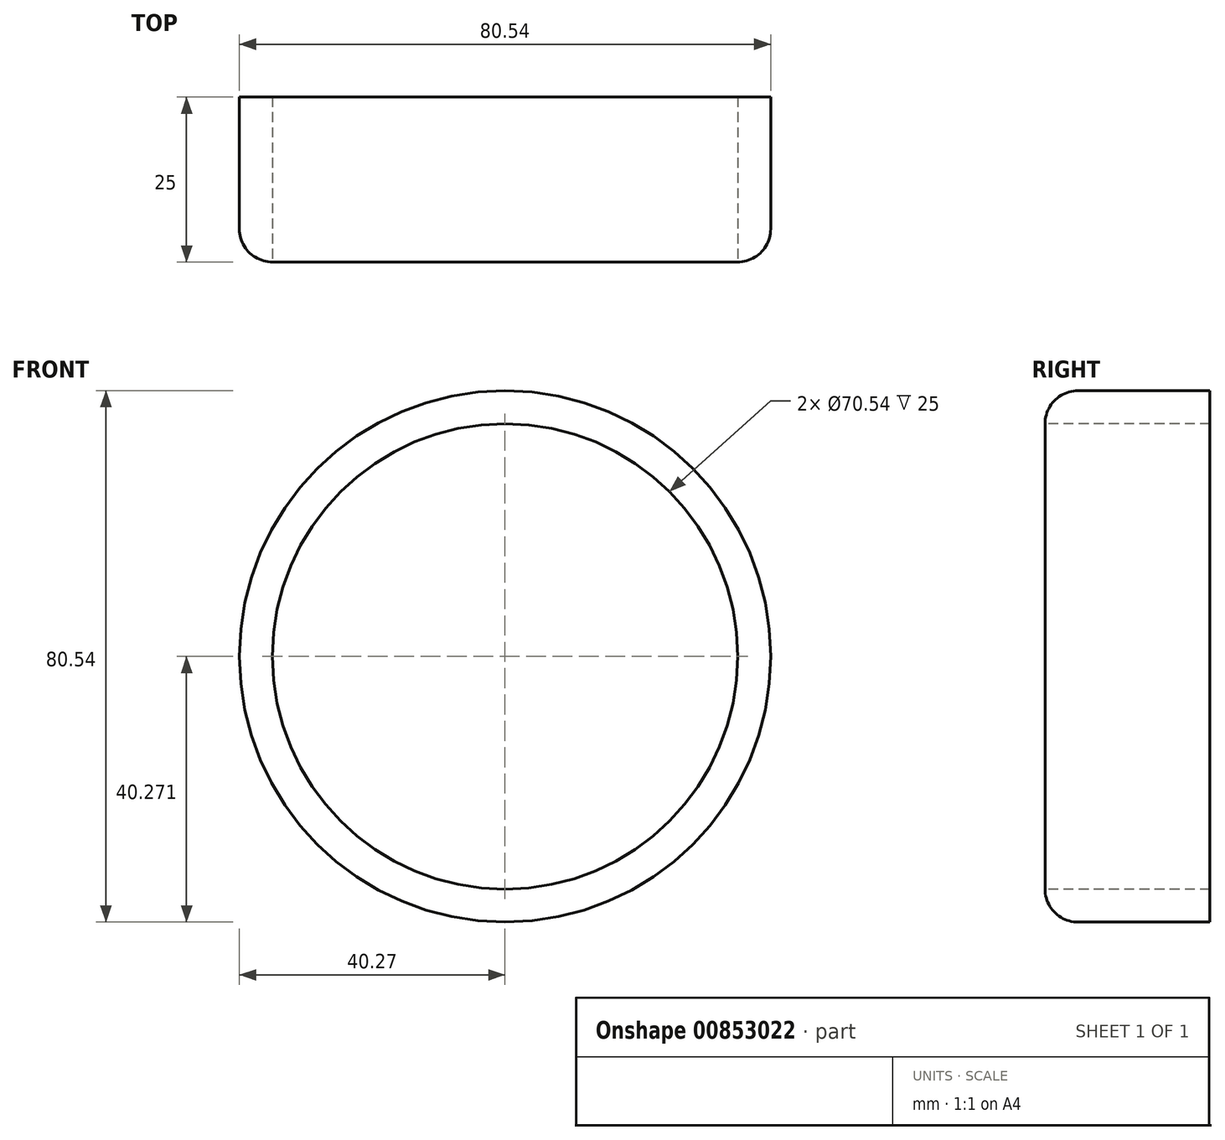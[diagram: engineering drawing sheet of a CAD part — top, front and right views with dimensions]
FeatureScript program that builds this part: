
annotation { "Feature Type Name" : "Feature", "Feature Type Description" : "" }
export const myFeature = defineFeature(function(context is Context, id is Id, definition is map)
    precondition{}
    {
        {
            var Q0;
            Q0=qCreatedBy(makeId("Front.planeOp"),FACE);
            var sketch = newSketch(context, id + "F0", { "sketchPlane" : qUnion([Q0])});
            skCircle(sketch, "E0", {"center": v(0, -5.18) * mm, "radius": 40.27 * mm});
            skSolve(sketch);
        }
        {
            var Q0;
            Q0 = qSketchRegion(id + "F0", true);
            extrude(context, id + "F1", {"entities" : qUnion([Q0]), "depth" : 25 * mm, "offsetDistance" : 25 * mm});
        }
        {
            var Q0;
            Q0=makeQuery(id+"F1.opExtrude","CAP_FACE",FACE,{"disambiguationData":[OSD([sQuery(id+"F0.wireOp",EDGE,"E0")])],"isStart":false});
            fillet(context, id + "F2", {"entities" : qUnion([Q0]), "radius" : 5 * mm, "tangentPropagation" : true, "allowEdgeOverflow" : false});
        }
        {
            var Q0;
            Q0=makeQuery(id+"F1.opExtrude","CAP_FACE",FACE,{"disambiguationData":[OSD([sQuery(id+"F0.wireOp",EDGE,"E0")])],"isStart":false});
            extrude(context, id + "F3", {"entities" : qUnion([Q0]), "operationType" : NewBodyOperationType.REMOVE, "oppositeDirection" : true, "depth" : 103 * mm, "offsetDistance" : 25 * mm});
        }
        {
            var Q0;
            Q0=makeQuery(id+"F1.opExtrude","SWEPT_BODY",BODY,{"disambiguationData":[OSD([sQuery(id+"F0.wireOp",EDGE,"E0")])]});
            transform(context, id + "F4", {"entities" : qUnion([Q0]), "transformType" : TransformType.TRANSLATION_3D, "dx" : 0 * mm, "dy" : 0 * mm, "dz" : 0 * mm, "makeCopy" : true});
        }
    });
